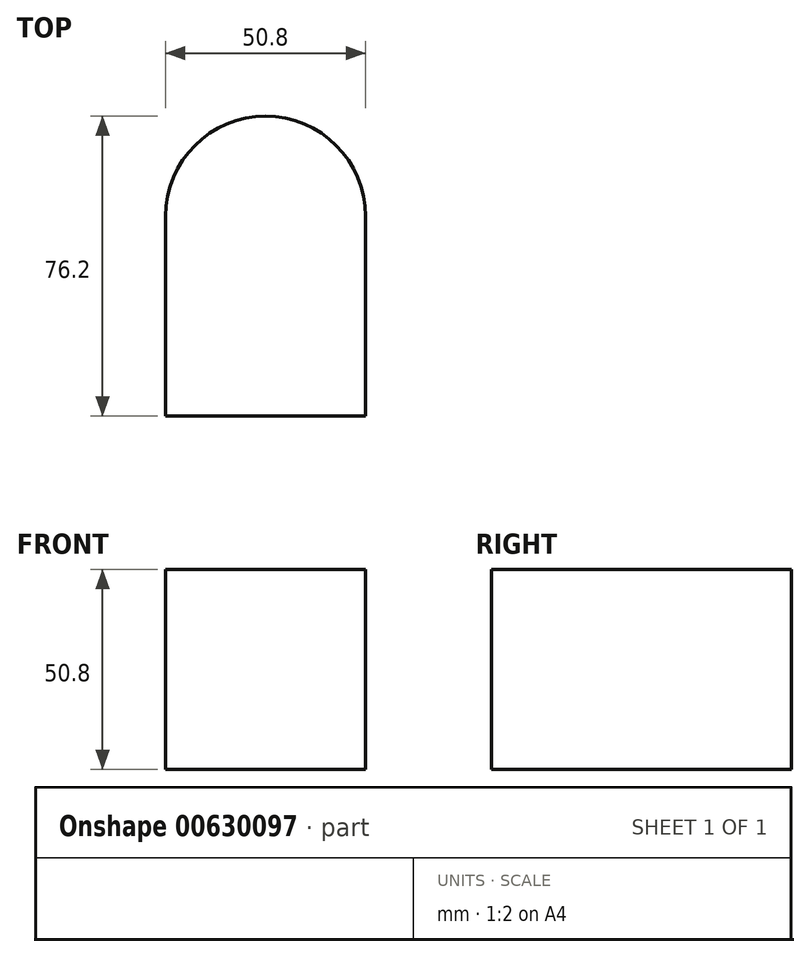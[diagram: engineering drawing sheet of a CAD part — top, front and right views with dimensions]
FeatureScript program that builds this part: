
annotation { "Feature Type Name" : "Feature", "Feature Type Description" : "" }
export const myFeature = defineFeature(function(context is Context, id is Id, definition is map)
    precondition{}
    {
        {
            var Q0;
            Q0=qCreatedBy(makeId("Top.planeOp"),FACE);
            var sketch = newSketch(context, id + "F0", { "sketchPlane" : qUnion([Q0])});
            skLineSegment(sketch, "E0.bottom", {"start": v(-25.81, 30.02) * mm, "end": v(24.99, 30.02) * mm});
            skLineSegment(sketch, "E0.top", {"start": v(-25.81, -20.78) * mm, "end": v(24.99, -20.78) * mm});
            skLineSegment(sketch, "E0.left", {"start": v(-25.81, 30.02) * mm, "end": v(-25.81, -20.78) * mm});
            skLineSegment(sketch, "E0.right", {"start": v(24.99, 30.02) * mm, "end": v(24.99, -20.78) * mm});
            skArc(sketch, "E1", {"start": v(24.99, 30.02) * mm, "mid": v(-0.41, 55.42) * mm, "end": v(-25.81, 30.02) * mm});
            skSolve(sketch);
        }
        {
            var Q0;
            Q0=makeQuery(id+"F0.imprint","IMPRINT",FACE,{"disambiguationData":[TD([[makeQuery(id+"F0.imprint","IMPRINT",EDGE,{"derivedFrom":sQuery(id+"F0.wireOp",EDGE,"E0.bottom")}),-1.0]])]});
            extrude(context, id + "F1", {"entities" : qUnion([Q0]), "depth" : 50.8 * mm, "offsetDistance" : 25.4 * mm});
        }
        {
            var Q0;
            Q0=makeQuery(id+"F0.imprint","IMPRINT",FACE,{"disambiguationData":[TD([[makeQuery(id+"F0.imprint","IMPRINT",EDGE,{"derivedFrom":sQuery(id+"F0.wireOp",EDGE,"E0.bottom")}),1.0]])]});
            extrude(context, id + "F2", {"entities" : qUnion([Q0]), "operationType" : NewBodyOperationType.ADD, "depth" : 50.8 * mm, "offsetDistance" : 25.4 * mm});
        }
    });
